# Revit family: Sink-Under_Mount-Lavatory-KOHLER-Ledges-K-2838
name_source: partatom
category: Plumbing Fixtures
revit_build: Autodesk Revit 2017 (Build: 20160225_1515(x64)
units: mm (PartAtom-declared; Revit-internal decimal feet)

## family parameters
Cut with Voids When Loaded = No
Host = Face
OmniClass Number = 23.31.13.00
OmniClass Title = Sinks
Part Type = Normal
Room Calculation Point = No
Round Connector Dimension = Use Diameter
Shared = No

## types (5) — shared parameters
ADA Compliant = Yes
Assembly Code = D2010400
CW Connection = No
Cold Water Inlet = Cold Water Inlet
Date Modified = 01/30/2020
Default Elevation = 34"
Description = Undermount Bathroom Sink
Drain Included = No
Environmental Product Declaration = https://www.us.kohler.com
HW Connection = No
Height = 6"
Hot Water Inlet = Hot Water Inlet
Length = 22 1/2"
Manufacturer = KOHLER Co.
MasterFormat 1995 = 15410
MasterFormat 2004 = 22.41.16
Material = Enameled Cast Iron
Product Documentation Link = https://www.us.kohler.com
Product Name = Ledges
Product Page URL = http://www.us.kohler.com
URL = https://www.us.kohler.com
Vent Connection = No
Waste Connection = Yes
Waste Water Outlet = Waste Water Outlet
WaterSense Certified = No
Width = 16 1/8"

## per-type parameters (varying)
| type | Finish | Model | Type |
| 0-White | KOHLER-Enameled_Cast_Iron-0-White | K-2838-0 | 1 |
| FF-Sea Salt | KOHLER-Enameled_Cast_Iron-FF-Sea_Salt | K-2838-FF | 2 |
| 96-Biscuit | KOHLER-Enameled_Cast_Iron-96-Biscuit | K-2838-96 | 3 |
| FT-Basalt | KOHLER-Enameled_Cast_Iron-FT-Basalt | K-2838-FT | 4 |
| KA-Black 'n Tan | KOHLER-Enameled_Cast_Iron-KA-Black_n_Tan | K-2838-KA | 5 |

## geometry (parser evidence)
native form markers: Sweep x6
no freeform markers — native parametric forms only
